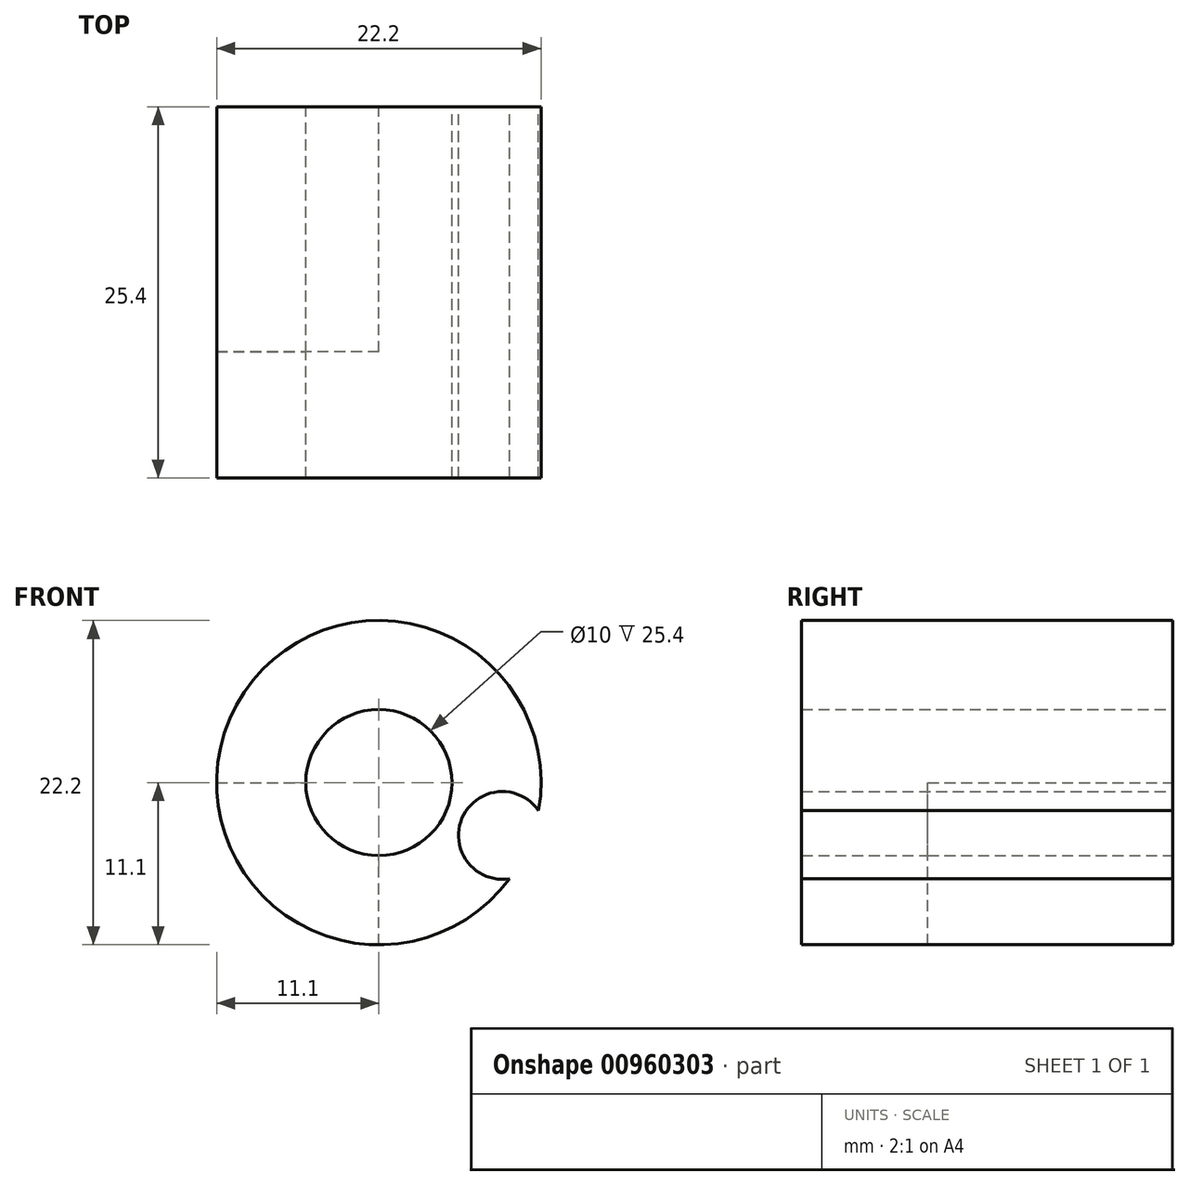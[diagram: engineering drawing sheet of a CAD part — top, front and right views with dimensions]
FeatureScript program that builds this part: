
annotation { "Feature Type Name" : "Feature", "Feature Type Description" : "" }
export const myFeature = defineFeature(function(context is Context, id is Id, definition is map)
    precondition{}
    {
        {
            var Q0;
            Q0=qCreatedBy(makeId("Front.planeOp"),FACE);
            var sketch = newSketch(context, id + "F0", { "sketchPlane" : qUnion([Q0])});
            skCircle(sketch, "E0", {"center": v(0, 0) * mm, "radius": 11.1 * mm});
            skCircle(sketch, "E1", {"center": v(0, 0) * mm, "radius": 5 * mm});
            skSolve(sketch);
        }
        {
            var Q0;
            Q0=makeQuery(id+"F0.imprint","IMPRINT",FACE,{"disambiguationData":[TD([[makeQuery(id+"F0.imprint","IMPRINT",EDGE,{"derivedFrom":sQuery(id+"F0.wireOp",EDGE,"E0")}),1.0]])]});
            extrude(context, id + "F1", {"entities" : qUnion([Q0]), "depth" : 25.4 * mm, "offsetDistance" : 25.4 * mm});
        }
        {
            var Q0;
            Q0=qCreatedBy(makeId("Right.planeOp"),FACE);
            var sketch = newSketch(context, id + "F2", { "sketchPlane" : qUnion([Q0])});
            skLineSegment(sketch, "E2.bottom", {"start": v(-16.78, -27.24) * mm, "end": v(0, -27.24) * mm});
            skLineSegment(sketch, "E2.top", {"start": v(-16.78, 0) * mm, "end": v(0, 0) * mm});
            skLineSegment(sketch, "E2.left", {"start": v(-16.78, -27.24) * mm, "end": v(-16.78, 0) * mm});
            skLineSegment(sketch, "E2.right", {"start": v(0, -27.24) * mm, "end": v(0, 0) * mm});
            skSolve(sketch);
        }
        {
            var Q0;
            Q0=makeQuery(id+"F2.imprint","IMPRINT",FACE,{"disambiguationData":[TD([[makeQuery(id+"F2.imprint","IMPRINT",EDGE,{"derivedFrom":sQuery(id+"F2.wireOp",EDGE,"E2.bottom")}),1.0]])]});
            extrude(context, id + "F3", {"entities" : qUnion([Q0]), "operationType" : NewBodyOperationType.REMOVE, "oppositeDirection" : true, "depth" : 76.2 * mm, "offsetDistance" : 25.4 * mm});
        }
        {
            var Q0;
            Q0=makeQuery(id+"F1.opExtrude","CAP_FACE",FACE,{"disambiguationData":[OSD([sQuery(id+"F0.wireOp",EDGE,"E0"),sQuery(id+"F0.wireOp",EDGE,"E1")])],"isStart":true});
            var sketch = newSketch(context, id + "F4", { "sketchPlane" : qUnion([Q0])});
            skCircle(sketch, "E3", {"center": v(-8.45, -3.61) * mm, "radius": 3 * mm});
            skSolve(sketch);
        }
        {
            var Q0;
            {var subQ0=sQuery(id+"F4.wireOp",EDGE,"E3");var subQ1=makeQuery(id+"F1.opExtrude","CAP_EDGE",EDGE,{"disambiguationData":[OSD([sQuery(id+"F0.wireOp",EDGE,"E0")])],"isStart":true});var subQ2=makeQuery(id+"F4.imprint","INTERSECT",VERTEX,{"disambiguationData":[OD(0.0)],"derivedFrom":[subQ1,subQ0]});Q0=makeQuery(id+"F4.imprint","IMPRINT",FACE,{"disambiguationData":[TD([[makeQuery(id+"F4.imprint","IMPRINT",EDGE,{"disambiguationData":[TD([[subQ2,-1.0]])],"derivedFrom":subQ0}),1.0]])]});}
            var Q1;
            {var subQ0=sQuery(id+"F4.wireOp",EDGE,"E3");var subQ1=makeQuery(id+"F1.opExtrude","CAP_EDGE",EDGE,{"disambiguationData":[OSD([sQuery(id+"F0.wireOp",EDGE,"E0")])],"isStart":true});var subQ2=makeQuery(id+"F4.imprint","INTERSECT",VERTEX,{"disambiguationData":[OD(0.0)],"derivedFrom":[subQ1,subQ0]});Q1=makeQuery(id+"F4.imprint","IMPRINT",FACE,{"disambiguationData":[TD([[makeQuery(id+"F4.imprint","IMPRINT",EDGE,{"disambiguationData":[TD([[subQ2,1.0]])],"derivedFrom":subQ0}),1.0]])]});}
            extrude(context, id + "F5", {"entities" : qUnion([Q0, Q1]), "operationType" : NewBodyOperationType.REMOVE, "endBound" : BoundingType.THROUGH_ALL, "oppositeDirection" : true, "depth" : 25 * mm, "offsetDistance" : 25 * mm});
        }
    });
